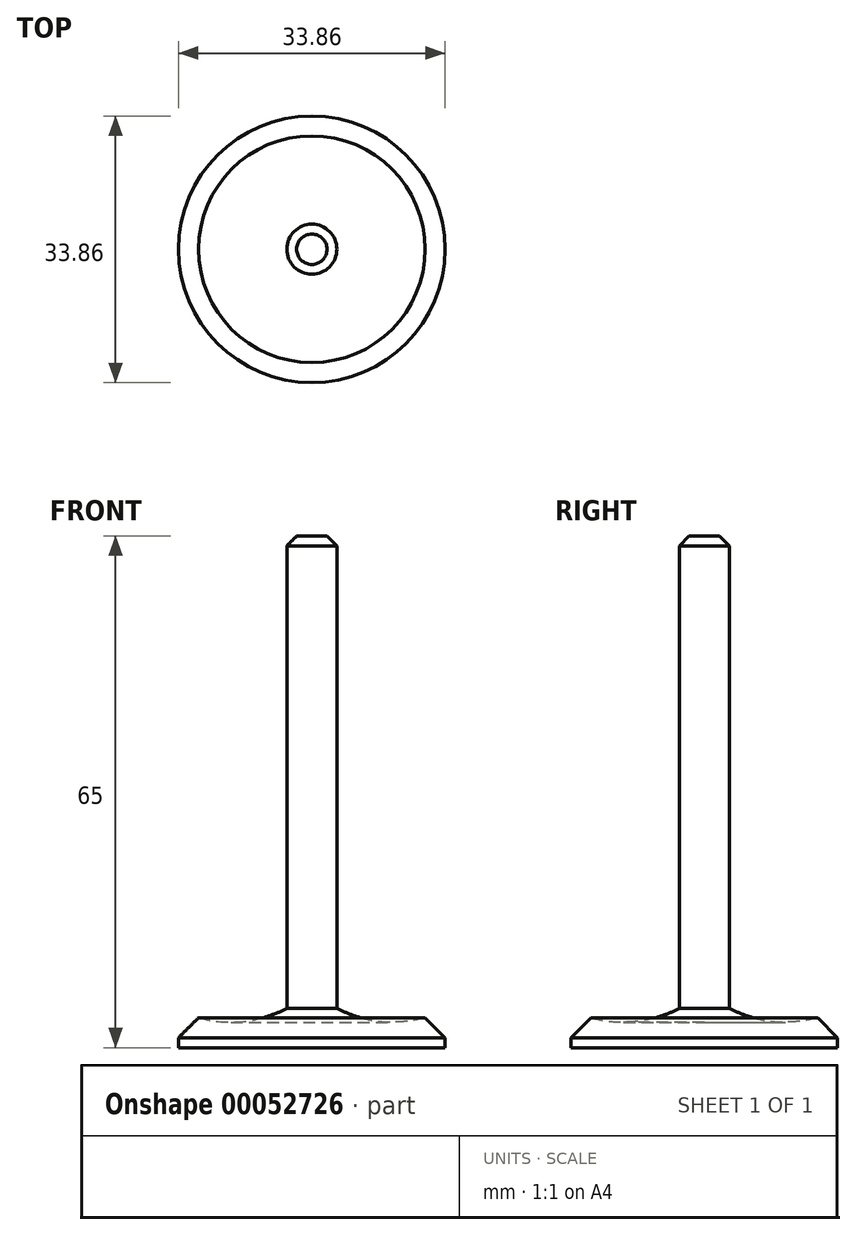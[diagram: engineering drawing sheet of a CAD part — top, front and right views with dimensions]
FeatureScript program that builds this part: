
annotation { "Feature Type Name" : "Feature", "Feature Type Description" : "" }
export const myFeature = defineFeature(function(context is Context, id is Id, definition is map)
    precondition{}
    {
        {
            var Q0;
            Q0=qCreatedBy(makeId("Front.planeOp"),FACE);
            var sketch = newSketch(context, id + "F0", { "sketchPlane" : qUnion([Q0])});
            skLineSegment(sketch, "E0", {"start": v(0, 0) * mm, "end": v(0, 65) * mm});
            skLineSegment(sketch, "E1", {"start": v(0, 65) * mm, "end": v(3.18, 65) * mm});
            skLineSegment(sketch, "E2", {"start": v(3.18, 65) * mm, "end": v(3.18, 5) * mm});
            skLineSegment(sketch, "E3", {"start": v(0, 0) * mm, "end": v(16.93, 0) * mm});
            skLineSegment(sketch, "E4", {"start": v(16.93, 0) * mm, "end": v(16.93, 1.27) * mm});
            skLineSegment(sketch, "E5", {"start": v(16.93, 1.27) * mm, "end": v(14.4, 3.81) * mm});
            skArc(sketch, "E6", {"start": v(3.18, 5) * mm, "mid": v(8.67, 3.33) * mm, "end": v(14.4, 3.81) * mm});
            skSolve(sketch);
        }
        {
            var Q0;
            Q0=makeQuery(id+"F0.imprint","IMPRINT",FACE,{"disambiguationData":[TD([[makeQuery(id+"F0.imprint","IMPRINT",EDGE,{"derivedFrom":sQuery(id+"F0.wireOp",EDGE,"E0")}),-1.0]])]});
            var Q1;
            Q1=sQuery(id+"F0.wireOp",EDGE,"E0");
            revolve(context, id + "F1", {"entities" : qUnion([Q0]), "axis" : qUnion([Q1]), "revolveType" : RevolveType.FULL});
        }
        {
            var Q0;
            Q0=makeQuery(id+"F1.opRevolve","SWEPT_EDGE",EDGE,{"disambiguationData":[OSD([sQuery(id+"F0.wireOp",EDGE,"E1"),sQuery(id+"F0.wireOp",EDGE,"E2")])]});
            chamfer(context, id + "F2", {"entities" : qUnion([Q0]), "chamferType" : ChamferType.OFFSET_ANGLE, "width" : 1.25 * mm, "oppositeDirection" : false, "angle" : 45 * degree, "tangentPropagation" : true});
        }
    });
